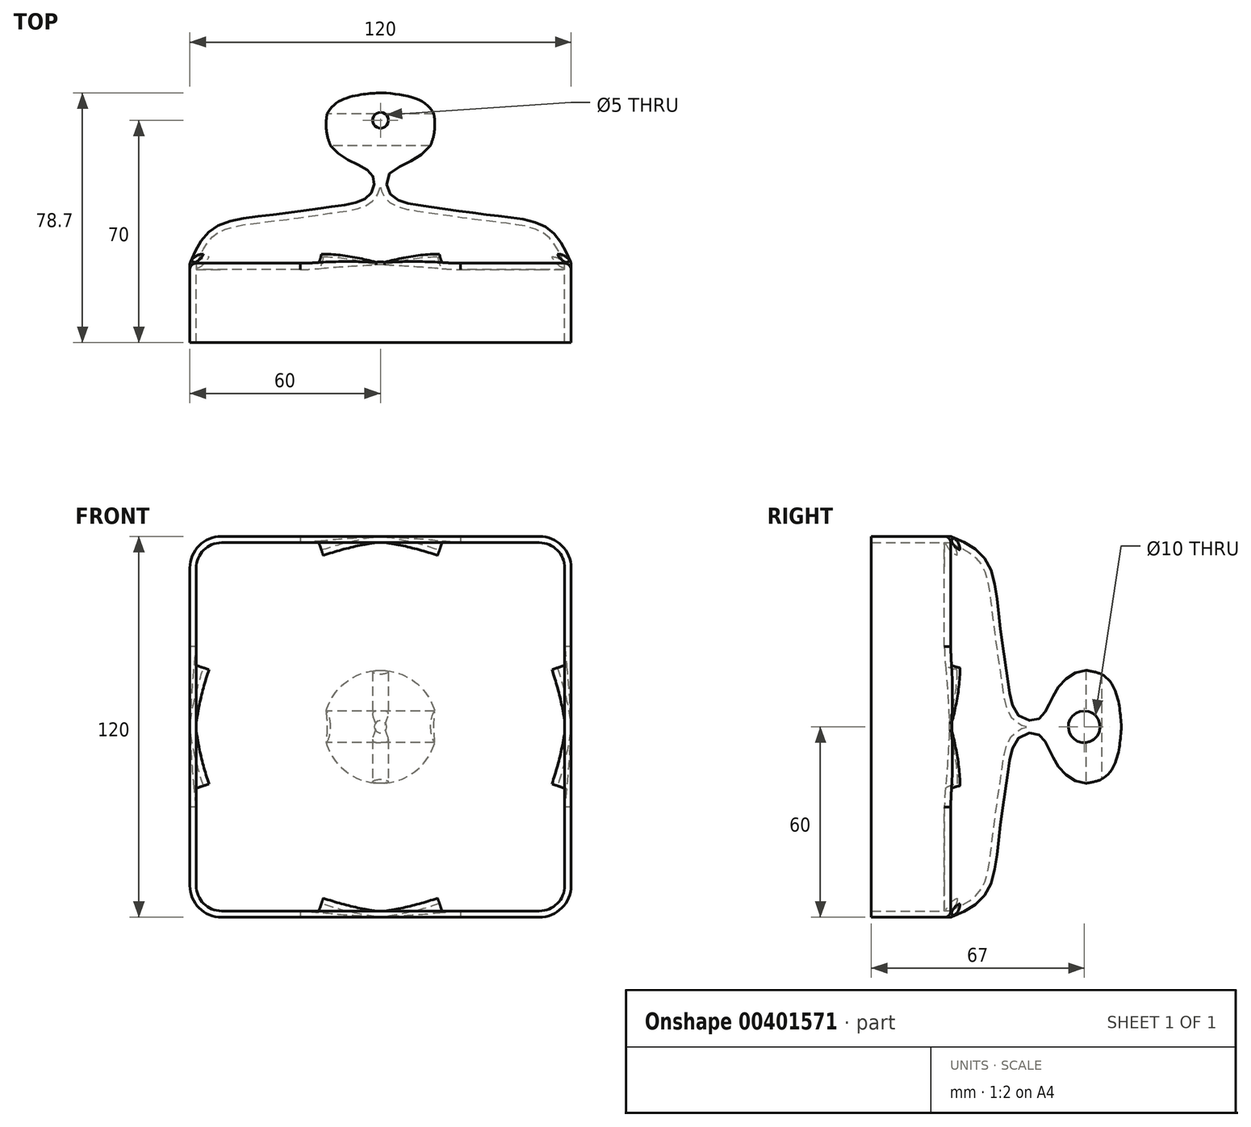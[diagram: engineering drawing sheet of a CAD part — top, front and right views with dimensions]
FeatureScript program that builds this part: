
annotation { "Feature Type Name" : "Feature", "Feature Type Description" : "" }
export const myFeature = defineFeature(function(context is Context, id is Id, definition is map)
    precondition{}
    {
        {
            var Q0;
            Q0=qCreatedBy(makeId("Front.planeOp"),FACE);
            var sketch = newSketch(context, id + "F0", { "sketchPlane" : qUnion([Q0])});
            skLineSegment(sketch, "E0.bottom", {"start": v(-60, 60) * mm, "end": v(60, 60) * mm});
            skLineSegment(sketch, "E0.top", {"start": v(-60, -60) * mm, "end": v(60, -60) * mm});
            skLineSegment(sketch, "E0.left", {"start": v(-60, 60) * mm, "end": v(-60, -60) * mm});
            skLineSegment(sketch, "E0.right", {"start": v(60, 60) * mm, "end": v(60, -60) * mm});
            skPoint(sketch, "E0.middle", {"position": v(0, 0) * mm});
            skSolve(sketch);
        }
        {
            var Q0;
            Q0 = qSketchRegion(id + "F0", true);
            extrude(context, id + "F1", {"entities" : qUnion([Q0]), "depth" : 25 * mm});
        }
        {
            var Q0;
            Q0=qCreatedBy(makeId("Top.planeOp"),FACE);
            var sketch = newSketch(context, id + "F2", { "sketchPlane" : qUnion([Q0])});
            skFitSpline(sketch, "E1", {"points": [v(-60, 0) * mm, v(-52.73, 10.95) * mm, v(-34.95, 15.14) * mm, v(-14.03, 18.01) * mm, v(-3.57, 21.28) * mm, v(-2.52, 27.69) * mm, v(-11.41, 33.18) * mm, v(-17.69, 41.55) * mm, v(-14.55, 49.91) * mm, v(-5.53, 53.18) * mm, v(0, 53.7) * mm], "startDerivative": vector(50.38, 116.6) * mm, "endDerivative": vector(71.1, 4.51) * mm});
            skFitSpline(sketch, "E2", {"points": [v(-1.68, 53.6) * mm, v(0, 53.7) * mm], "startDerivative": vector(1.68, 0.1) * mm, "endDerivative": vector(1.68, 0.1) * mm});
            skLineSegment(sketch, "E3", {"start": v(0, 53.7) * mm, "end": v(0, 0) * mm});
            skLineSegment(sketch, "E4", {"start": v(0, 0) * mm, "end": v(-60, 0) * mm});
            skSolve(sketch);
        }
        {
            var Q0;
            {var subQ0=sQuery(id+"F2.wireOp",EDGE,"E1");Q0=makeQuery(id+"F2.imprint","IMPRINT",FACE,{"disambiguationData":[TD([[makeQuery(id+"F2.imprint","IMPRINT",EDGE,{"derivedFrom":subQ0}),-1.0]])]});}
            var Q1;
            Q1=sQuery(id+"F2.wireOp",EDGE,"E3");
            revolve(context, id + "F3", {"operationType" : NewBodyOperationType.ADD, "entities" : qUnion([Q0]), "axis" : qUnion([Q1]), "revolveType" : RevolveType.FULL});
        }
        {
            var Q0;
            {var subQ0=sQuery(id+"F0.wireOp",EDGE,"E0.bottom");var subQ1=sQuery(id+"F2.wireOp",EDGE,"E1");var subQ2=sQuery(id+"F0.wireOp",EDGE,"E0.left");Q0=makeQuery(id+"F3.boolean.opBoolean","SPLIT",EDGE,{"disambiguationData":[TD([makeQuery(id+"F1.opExtrude","SWEPT_FACE",FACE,{"disambiguationData":[OSD([subQ0])]}),makeQuery(id+"F1.opExtrude","CAP_FACE",FACE,{"disambiguationData":[OSD([subQ0,sQuery(id+"F0.wireOp",EDGE,"E0.top"),subQ2,sQuery(id+"F0.wireOp",EDGE,"E0.right")])],"isStart":true}),makeQuery(id+"F1.opExtrude","SWEPT_FACE",FACE,{"disambiguationData":[OSD([subQ2])]}),makeQuery(id+"F3.opRevolve","SWEPT_FACE",FACE,{"disambiguationData":[OSD([subQ1])]})])],"derivedFrom":makeQuery(id+"F3.opRevolve","SWEPT_EDGE",EDGE,{"disambiguationData":[OSD([subQ1,sQuery(id+"F2.wireOp",EDGE,"E4")])]})});}
            var Q1;
            {var subQ0=sQuery(id+"F0.wireOp",EDGE,"E0.bottom");var subQ1=sQuery(id+"F0.wireOp",EDGE,"E0.right");var subQ2=sQuery(id+"F2.wireOp",EDGE,"E1");Q1=makeQuery(id+"F3.boolean.opBoolean","SPLIT",EDGE,{"disambiguationData":[TD([makeQuery(id+"F1.opExtrude","SWEPT_FACE",FACE,{"disambiguationData":[OSD([subQ0])]}),makeQuery(id+"F1.opExtrude","CAP_FACE",FACE,{"disambiguationData":[OSD([subQ0,sQuery(id+"F0.wireOp",EDGE,"E0.top"),sQuery(id+"F0.wireOp",EDGE,"E0.left"),subQ1])],"isStart":true}),makeQuery(id+"F1.opExtrude","SWEPT_FACE",FACE,{"disambiguationData":[OSD([subQ1])]}),makeQuery(id+"F3.opRevolve","SWEPT_FACE",FACE,{"disambiguationData":[OSD([subQ2])]})])],"derivedFrom":makeQuery(id+"F3.opRevolve","SWEPT_EDGE",EDGE,{"disambiguationData":[OSD([subQ2,sQuery(id+"F2.wireOp",EDGE,"E4")])]})});}
            var Q2;
            {var subQ0=sQuery(id+"F0.wireOp",EDGE,"E0.right");var subQ1=sQuery(id+"F0.wireOp",EDGE,"E0.top");var subQ2=sQuery(id+"F2.wireOp",EDGE,"E1");Q2=makeQuery(id+"F3.boolean.opBoolean","SPLIT",EDGE,{"disambiguationData":[TD([makeQuery(id+"F1.opExtrude","CAP_FACE",FACE,{"disambiguationData":[OSD([sQuery(id+"F0.wireOp",EDGE,"E0.bottom"),subQ1,sQuery(id+"F0.wireOp",EDGE,"E0.left"),subQ0])],"isStart":true}),makeQuery(id+"F1.opExtrude","SWEPT_FACE",FACE,{"disambiguationData":[OSD([subQ1])]}),makeQuery(id+"F1.opExtrude","SWEPT_FACE",FACE,{"disambiguationData":[OSD([subQ0])]}),makeQuery(id+"F3.opRevolve","SWEPT_FACE",FACE,{"disambiguationData":[OSD([subQ2])]})])],"derivedFrom":makeQuery(id+"F3.opRevolve","SWEPT_EDGE",EDGE,{"disambiguationData":[OSD([subQ2,sQuery(id+"F2.wireOp",EDGE,"E4")])]})});}
            fillet(context, id + "F4", {"entities" : qUnion([Q0, Q1, Q2]), "radius" : 5 * mm, "tangentPropagation" : true, "allowEdgeOverflow" : false});
        }
        {
            var Q0;
            {var subQ0=sQuery(id+"F0.wireOp",EDGE,"E0.bottom");var subQ1=sQuery(id+"F0.wireOp",EDGE,"E0.left");Q0=makeQuery(id+"F3.boolean.opBoolean","SPLIT",EDGE,{"disambiguationData":[TD([makeQuery(id+"F1.opExtrude","SWEPT_FACE",FACE,{"disambiguationData":[OSD([subQ0])]})])],"derivedFrom":makeQuery(id+"F1.opExtrude","CAP_EDGE",EDGE,{"disambiguationData":[OSD([subQ1])],"isStart":true})});}
            var Q1;
            {var subQ0=sQuery(id+"F0.wireOp",EDGE,"E0.left");var subQ1=sQuery(id+"F0.wireOp",EDGE,"E0.top");Q1=makeQuery(id+"F3.boolean.opBoolean","SPLIT",EDGE,{"disambiguationData":[TD([makeQuery(id+"F1.opExtrude","SWEPT_FACE",FACE,{"disambiguationData":[OSD([subQ1])]})])],"derivedFrom":makeQuery(id+"F1.opExtrude","CAP_EDGE",EDGE,{"disambiguationData":[OSD([subQ0])],"isStart":true})});}
            var Q2;
            {var subQ0=sQuery(id+"F0.wireOp",EDGE,"E0.left");var subQ1=sQuery(id+"F0.wireOp",EDGE,"E0.top");Q2=makeQuery(id+"F3.boolean.opBoolean","SPLIT",EDGE,{"disambiguationData":[TD([makeQuery(id+"F1.opExtrude","SWEPT_FACE",FACE,{"disambiguationData":[OSD([subQ0])]})])],"derivedFrom":makeQuery(id+"F1.opExtrude","CAP_EDGE",EDGE,{"disambiguationData":[OSD([subQ1])],"isStart":true})});}
            var Q3;
            {var subQ0=sQuery(id+"F0.wireOp",EDGE,"E0.right");var subQ1=sQuery(id+"F0.wireOp",EDGE,"E0.top");Q3=makeQuery(id+"F3.boolean.opBoolean","SPLIT",EDGE,{"disambiguationData":[TD([makeQuery(id+"F1.opExtrude","SWEPT_FACE",FACE,{"disambiguationData":[OSD([subQ0])]})])],"derivedFrom":makeQuery(id+"F1.opExtrude","CAP_EDGE",EDGE,{"disambiguationData":[OSD([subQ1])],"isStart":true})});}
            var Q4;
            {var subQ0=sQuery(id+"F0.wireOp",EDGE,"E0.right");var subQ1=sQuery(id+"F0.wireOp",EDGE,"E0.top");Q4=makeQuery(id+"F3.boolean.opBoolean","SPLIT",EDGE,{"disambiguationData":[TD([makeQuery(id+"F1.opExtrude","SWEPT_FACE",FACE,{"disambiguationData":[OSD([subQ1])]})])],"derivedFrom":makeQuery(id+"F1.opExtrude","CAP_EDGE",EDGE,{"disambiguationData":[OSD([subQ0])],"isStart":true})});}
            var Q5;
            {var subQ0=sQuery(id+"F0.wireOp",EDGE,"E0.bottom");var subQ1=sQuery(id+"F0.wireOp",EDGE,"E0.right");Q5=makeQuery(id+"F3.boolean.opBoolean","SPLIT",EDGE,{"disambiguationData":[TD([makeQuery(id+"F1.opExtrude","SWEPT_FACE",FACE,{"disambiguationData":[OSD([subQ0])]})])],"derivedFrom":makeQuery(id+"F1.opExtrude","CAP_EDGE",EDGE,{"disambiguationData":[OSD([subQ1])],"isStart":true})});}
            var Q6;
            {var subQ0=sQuery(id+"F0.wireOp",EDGE,"E0.bottom");var subQ1=sQuery(id+"F0.wireOp",EDGE,"E0.right");Q6=makeQuery(id+"F3.boolean.opBoolean","SPLIT",EDGE,{"disambiguationData":[TD([makeQuery(id+"F1.opExtrude","SWEPT_FACE",FACE,{"disambiguationData":[OSD([subQ1])]})])],"derivedFrom":makeQuery(id+"F1.opExtrude","CAP_EDGE",EDGE,{"disambiguationData":[OSD([subQ0])],"isStart":true})});}
            var Q7;
            {var subQ0=sQuery(id+"F0.wireOp",EDGE,"E0.bottom");var subQ1=sQuery(id+"F0.wireOp",EDGE,"E0.left");Q7=makeQuery(id+"F3.boolean.opBoolean","SPLIT",EDGE,{"disambiguationData":[TD([makeQuery(id+"F1.opExtrude","SWEPT_FACE",FACE,{"disambiguationData":[OSD([subQ1])]})])],"derivedFrom":makeQuery(id+"F1.opExtrude","CAP_EDGE",EDGE,{"disambiguationData":[OSD([subQ0])],"isStart":true})});}
            fillet(context, id + "F5", {"entities" : qUnion([Q0, Q1, Q2, Q3, Q4, Q5, Q6, Q7]), "radius" : 2 * mm, "tangentPropagation" : true, "allowEdgeOverflow" : false});
        }
        {
            var Q0;
            Q0=makeQuery(id+"F1.opExtrude","SWEPT_EDGE",EDGE,{"disambiguationData":[OSD([sQuery(id+"F0.wireOp",EDGE,"E0.bottom"),sQuery(id+"F0.wireOp",EDGE,"E0.right")])]});
            var Q1;
            Q1=makeQuery(id+"F1.opExtrude","SWEPT_EDGE",EDGE,{"disambiguationData":[OSD([sQuery(id+"F0.wireOp",EDGE,"E0.top"),sQuery(id+"F0.wireOp",EDGE,"E0.right")])]});
            var Q2;
            Q2=makeQuery(id+"F1.opExtrude","SWEPT_EDGE",EDGE,{"disambiguationData":[OSD([sQuery(id+"F0.wireOp",EDGE,"E0.bottom"),sQuery(id+"F0.wireOp",EDGE,"E0.left")])]});
            var Q3;
            Q3=makeQuery(id+"F1.opExtrude","SWEPT_EDGE",EDGE,{"disambiguationData":[OSD([sQuery(id+"F0.wireOp",EDGE,"E0.top"),sQuery(id+"F0.wireOp",EDGE,"E0.left")])]});
            fillet(context, id + "F6", {"entities" : qUnion([Q0, Q1, Q2, Q3]), "radius" : 10 * mm, "tangentPropagation" : true, "allowEdgeOverflow" : false});
        }
        {
            var Q0;
            Q0=makeQuery(id+"F1.opExtrude","CAP_FACE",FACE,{"disambiguationData":[OSD([sQuery(id+"F0.wireOp",EDGE,"E0.bottom"),sQuery(id+"F0.wireOp",EDGE,"E0.top"),sQuery(id+"F0.wireOp",EDGE,"E0.left"),sQuery(id+"F0.wireOp",EDGE,"E0.right")])],"isStart":false});
            shell(context, id + "F7", {"entities" : qUnion([Q0]), "thickness" : 2 * mm});
        }
        {
            var Q0;
            Q0=qCreatedBy(makeId("Top.planeOp"),FACE);
            var sketch = newSketch(context, id + "F8", { "sketchPlane" : qUnion([Q0])});
            skCircle(sketch, "E5", {"center": v(0, 45) * mm, "radius": 2.5 * mm});
            skSolve(sketch);
        }
        {
            var Q0;
            Q0 = qSketchRegion(id + "F8", true);
            extrude(context, id + "F9", {"entities" : qUnion([Q0]), "operationType" : NewBodyOperationType.REMOVE, "endBound" : BoundingType.THROUGH_ALL, "depth" : 25 * mm, "hasSecondDirection" : true, "secondDirectionBound" : SecondDirectionBoundingType.THROUGH_ALL, "secondDirectionOppositeDirection" : true, "secondDirectionDepth" : 25 * mm});
        }
        {
            var Q0;
            Q0=qCreatedBy(makeId("Right.planeOp"),FACE);
            var sketch = newSketch(context, id + "F10", { "sketchPlane" : qUnion([Q0])});
            skCircle(sketch, "E6", {"center": v(42, 0) * mm, "radius": 5 * mm});
            skSolve(sketch);
        }
        {
            var Q0;
            Q0 = qSketchRegion(id + "F10", true);
            extrude(context, id + "F11", {"entities" : qUnion([Q0]), "operationType" : NewBodyOperationType.REMOVE, "endBound" : BoundingType.THROUGH_ALL, "depth" : 25 * mm, "hasSecondDirection" : true, "secondDirectionBound" : SecondDirectionBoundingType.THROUGH_ALL, "secondDirectionOppositeDirection" : true, "secondDirectionDepth" : 25 * mm});
        }
    });
